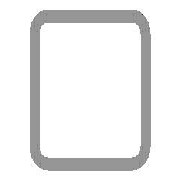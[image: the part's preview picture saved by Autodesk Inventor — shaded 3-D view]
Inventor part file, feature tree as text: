
AUTODESK INVENTOR PART (.ipt)
format: ipt  version: 2018 (Build 220112000, 112)  size: 130,048 bytes
history: native  units: mm (DEFAULTED — no unit token found)
features: other x3, sketch x3, extrude x1, plane x1
ambient origin geometry x8: Origin, YZ Plane, XZ Plane, XY Plane, X Axis, Y Axis, Z Axis, Center Point
bodies: Solid1 (feature_tree)
feature tree (8):
  other  "Driven Length"
  other  "Piano iniziale"
  other  "Piano finale"
  extrude  "Corpo"  TaperAngle=0.0deg  [1 undecoded]
  sketch  "Schizzo"
  sketch  "Sketch3"  dims[d3=260.0mm d4=0.0mm]
  plane  "Work Plane3"
  sketch  "Sketch4"  dims[d7=4.0mm d9=20.0mm d11=20.0mm d12=2.0mm d13=-0.0mm d14=260.0mm d15=10.0mm d16=10.0mm d17=90.0deg d18=260.0mm]
note: 1 required parameter value undecoded (feature->parameter linkage not recoverable at this tier; creation-order binding heuristic only, values carry confidence <= 0.55)
